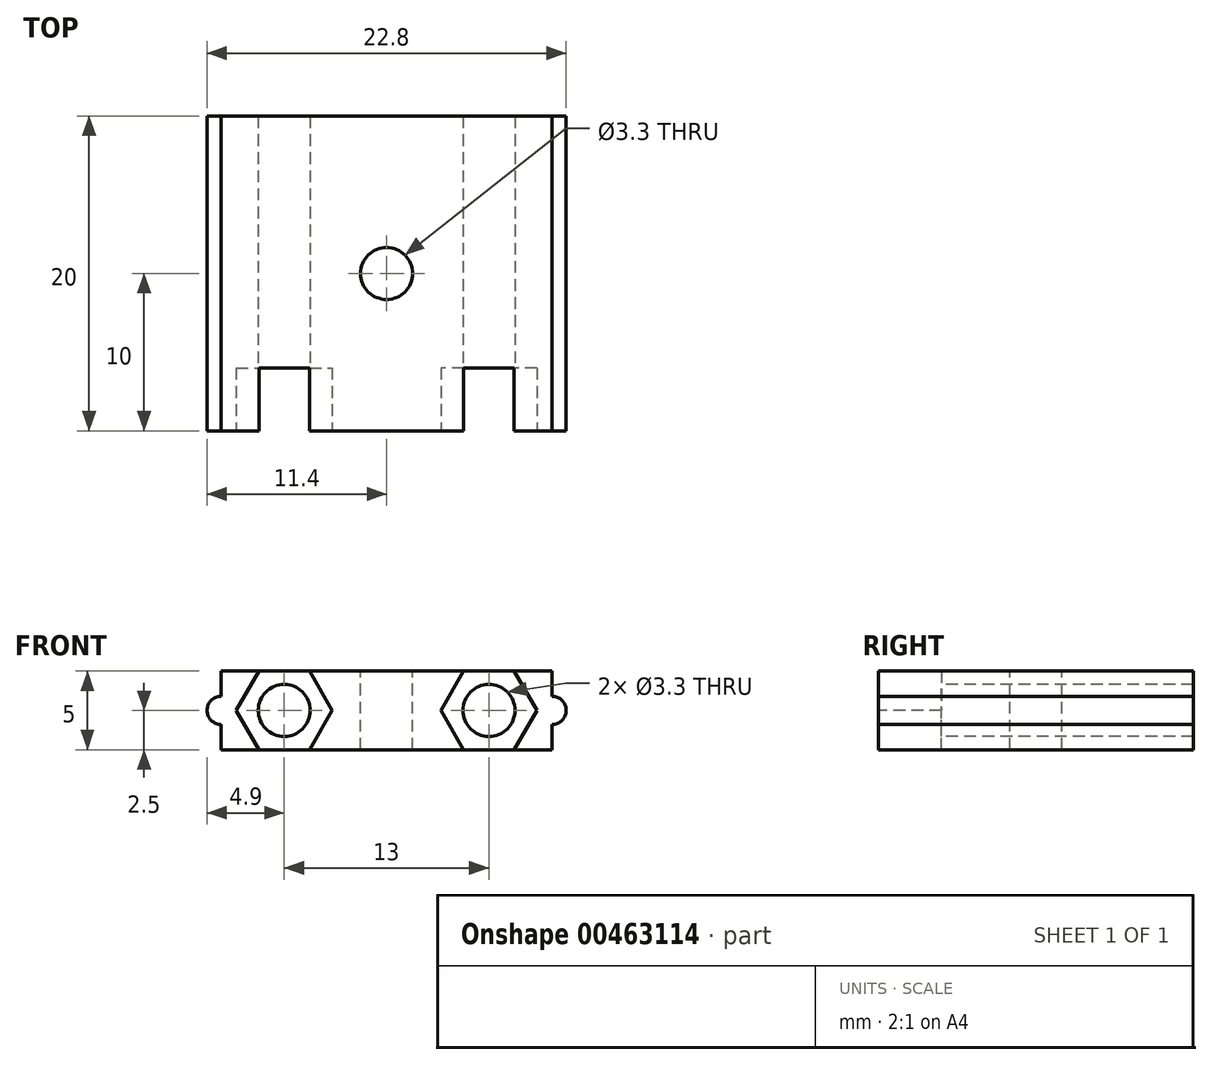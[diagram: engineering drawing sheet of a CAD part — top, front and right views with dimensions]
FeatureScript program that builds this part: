
annotation { "Feature Type Name" : "Feature", "Feature Type Description" : "" }
export const myFeature = defineFeature(function(context is Context, id is Id, definition is map)
    precondition{}
    {
        {
            var Q0;
            Q0=qCreatedBy(makeId("Front.planeOp"),FACE);
            var sketch = newSketch(context, id + "F0", { "sketchPlane" : qUnion([Q0])});
            skLineSegment(sketch, "E0.bottom", {"start": v(10.5, 2.5) * mm, "end": v(-10.5, 2.5) * mm});
            skLineSegment(sketch, "E0.top", {"start": v(10.5, -2.5) * mm, "end": v(-10.5, -2.5) * mm});
            skLineSegment(sketch, "E0.left", {"start": v(10.5, 2.5) * mm, "end": v(10.5, -2.5) * mm});
            skLineSegment(sketch, "E0.right", {"start": v(-10.5, 2.5) * mm, "end": v(-10.5, -2.5) * mm});
            skPoint(sketch, "E0.middle", {"position": v(0, 0) * mm});
            skPoint(sketch, "E1", {"position": v(-10.5, -0.9) * mm});
            skPoint(sketch, "E2.0.1.0", {"position": v(-10.5, 0) * mm});
            skPoint(sketch, "E2.1.0.0", {"position": v(0, -0.9) * mm});
            skPoint(sketch, "E2.2.0.0", {"position": v(10.5, -0.9) * mm});
            skPoint(sketch, "E2.2.1.0", {"position": v(10.5, 0) * mm});
            skLineSegment(sketch, "E2.direction1", {"start": v(-10.5, -0.9) * mm, "end": v(0, -0.9) * mm, "construction": true});
            skLineSegment(sketch, "E2.direction2", {"start": v(-10.5, -0.9) * mm, "end": v(-10.5, 0) * mm, "construction": true});
            skPoint(sketch, "E3.0.0.2", {"position": v(-10.5, 0.9) * mm});
            skPoint(sketch, "E3.0.1.2", {"position": v(0, 0.9) * mm});
            skPoint(sketch, "E3.0.2.2", {"position": v(10.5, 0.9) * mm});
            skArc(sketch, "E4", {"start": v(-10.5, 0.9) * mm, "mid": v(-11.4, 0) * mm, "end": v(-10.5, -0.9) * mm});
            skArc(sketch, "E5.MirrorCS", {"start": v(10.5, 0.9) * mm, "mid": v(11.4, 0) * mm, "end": v(10.5, -0.9) * mm});
            skPoint(sketch, "E6", {"position": v(-6.5, 0) * mm});
            skPoint(sketch, "E7.MirrorP", {"position": v(6.5, 0) * mm});
            skSolve(sketch);
        }
        {
            var Q0;
            Q0 = qSketchRegion(id + "F0", true);
            extrude(context, id + "F1", {"entities" : qUnion([Q0]), "endBound" : BoundingType.SYMMETRIC, "depth" : 20 * mm});
        }
        {
            var Q0;
            Q0=makeQuery(id+"F1.opExtrude","SWEPT_FACE",FACE,{"disambiguationData":[OSD([sQuery(id+"F0.wireOp",EDGE,"E0.bottom")])]});
            var sketch = newSketch(context, id + "F2", { "sketchPlane" : qUnion([Q0])});
            skPoint(sketch, "E8", {"position": v(0, 0) * mm});
            skSolve(sketch);
        }
        {
            var Q0;
            Q0=sQuery(id+"F2.wireOp",VERTEX,"E8");
            var Q1;
            Q1=makeQuery(id+"F1.opExtrude","SWEPT_BODY",BODY,{"disambiguationData":[OSD([sQuery(id+"F0.wireOp",EDGE,"E0.bottom"),sQuery(id+"F0.wireOp",EDGE,"E0.top"),sQuery(id+"F0.wireOp",EDGE,"E0.left"),sQuery(id+"F0.wireOp",EDGE,"E0.right"),sQuery(id+"F0.wireOp",EDGE,"E4"),sQuery(id+"F0.wireOp",EDGE,"E5.MirrorCS")])]});
            hole(context, id + "F3", {"style" : HoleStyle.SIMPLE, "endStyle" : HoleEndStyle.THROUGH, "standardTappedOrClearance" : lookupTablePath({ "standard" : "ISO", "fit" : "Normal", "size" : "M3", "type" : "Clearance" }), "standardBlindInLast" : lookupTablePath({ "fit" : "Standard", "standard" : "ISO", "size" : "M3", "type" : "Clearance" }), "holeDiameter" : 3.3 * mm, "isTappedThrough" : true, "tappedDepth" : 12 * mm, "tapClearance" : 3, "locations" : qUnion([Q0]), "scope" : qUnion([Q1])});
        }
        {
            var Q0;
            Q0=makeQuery(id+"F1.opExtrude","CAP_FACE",FACE,{"disambiguationData":[OSD([sQuery(id+"F0.wireOp",EDGE,"E0.bottom"),sQuery(id+"F0.wireOp",EDGE,"E0.top"),sQuery(id+"F0.wireOp",EDGE,"E0.left"),sQuery(id+"F0.wireOp",EDGE,"E0.right"),sQuery(id+"F0.wireOp",EDGE,"E4"),sQuery(id+"F0.wireOp",EDGE,"E5.MirrorCS")])],"isStart":false});
            var sketch = newSketch(context, id + "F4", { "sketchPlane" : qUnion([Q0])});
            skPoint(sketch, "E9", {"position": v(-6.5, 0) * mm});
            skCircle(sketch, "E10.cCircle", {"center": v(-6.5, 0) * mm, "radius": 2.64 * mm, "construction": true});
            skLineSegment(sketch, "E10.0", {"start": v(-4.98, 2.64) * mm, "end": v(-3.45, 0) * mm});
            skLineSegment(sketch, "E10.1", {"start": v(-3.45, 0) * mm, "end": v(-4.98, -2.64) * mm});
            skLineSegment(sketch, "E10.2", {"start": v(-4.98, -2.64) * mm, "end": v(-8.03, -2.64) * mm});
            skLineSegment(sketch, "E10.3", {"start": v(-8.02, -2.64) * mm, "end": v(-9.55, 0) * mm});
            skLineSegment(sketch, "E10.4", {"start": v(-9.55, 0) * mm, "end": v(-8.02, 2.64) * mm});
            skLineSegment(sketch, "E10.5", {"start": v(-8.02, 2.64) * mm, "end": v(-4.97, 2.64) * mm});
            skPoint(sketch, "E10.0.midPoint", {"position": v(-4.21, 1.32) * mm});
            skLineSegment(sketch, "E11.MirrorCS", {"start": v(3.45, 0) * mm, "end": v(4.98, -2.64) * mm});
            skLineSegment(sketch, "E12.MirrorCS", {"start": v(4.98, 2.64) * mm, "end": v(3.45, 0) * mm});
            skPoint(sketch, "E13.MirrorP", {"position": v(6.5, 0) * mm});
            skCircle(sketch, "E14.MirrorC", {"center": v(6.5, 0) * mm, "radius": 2.64 * mm, "construction": true});
            skPoint(sketch, "E15.MirrorP", {"position": v(4.21, 1.32) * mm});
            skLineSegment(sketch, "E16.MirrorCS", {"start": v(8.02, 2.64) * mm, "end": v(4.97, 2.64) * mm});
            skLineSegment(sketch, "E17.MirrorCS", {"start": v(8.02, -2.64) * mm, "end": v(9.55, 0) * mm});
            skLineSegment(sketch, "E18.MirrorCS", {"start": v(4.98, -2.64) * mm, "end": v(8.03, -2.64) * mm});
            skLineSegment(sketch, "E19.MirrorCS", {"start": v(9.55, 0) * mm, "end": v(8.02, 2.64) * mm});
            skLineSegment(sketch, "E20", {"start": v(0, -2.5) * mm, "end": v(0, 2.5) * mm, "construction": true});
            skSolve(sketch);
        }
        {
            var Q0;
            Q0=sQuery(id+"F4.wireOp",VERTEX,"E9");
            var Q1;
            Q1=sQuery(id+"F4.wireOp",VERTEX,"E13.MirrorP");
            var Q2;
            Q2=makeQuery(id+"F1.opExtrude","SWEPT_BODY",BODY,{"disambiguationData":[OSD([sQuery(id+"F0.wireOp",EDGE,"E0.bottom"),sQuery(id+"F0.wireOp",EDGE,"E0.top"),sQuery(id+"F0.wireOp",EDGE,"E0.left"),sQuery(id+"F0.wireOp",EDGE,"E0.right"),sQuery(id+"F0.wireOp",EDGE,"E4"),sQuery(id+"F0.wireOp",EDGE,"E5.MirrorCS")])]});
            hole(context, id + "F5", {"style" : HoleStyle.SIMPLE, "endStyle" : HoleEndStyle.THROUGH, "standardTappedOrClearance" : lookupTablePath({ "standard" : "ISO", "fit" : "Normal", "size" : "M3", "type" : "Clearance" }), "standardBlindInLast" : lookupTablePath({ "fit" : "Standard", "standard" : "ISO", "size" : "M3", "type" : "Clearance" }), "holeDiameter" : 3.3 * mm, "isTappedThrough" : true, "tappedDepth" : 12 * mm, "tapClearance" : 3, "locations" : qUnion([Q0, Q1]), "scope" : qUnion([Q2])});
        }
        {
            var Q0;
            Q0 = qSketchRegion(id + "F4", true);
            extrude(context, id + "F6", {"entities" : qUnion([Q0]), "operationType" : NewBodyOperationType.REMOVE, "oppositeDirection" : true, "depth" : 4 * mm});
        }
    });
